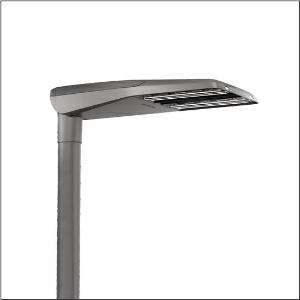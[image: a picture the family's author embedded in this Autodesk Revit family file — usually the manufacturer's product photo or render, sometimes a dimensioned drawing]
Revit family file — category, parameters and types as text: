
# Revit family: streetlight_sl_11_iq_midi___st1_2p1_0_5xc3g41e08me_f4ca
name_source: partatom
category: Lighting Fixtures
units: mm (PartAtom-declared; Revit-internal decimal feet)

## family parameters
Cut with Voids When Loaded = No
Host = Face
Light Source = No
Part Type = Normal
Room Calculation Point = No
Round Connector Dimension = Use Diameter
Shared = No

## types (1)
- --- (1 x LED, 18520 lm, 121.7 W, 4000K)
    Apparent Load = 122 VA
    CIE Flux Codes = 31 68 95 100 100
    Color Rendering = 70
    Color Temperature = 4000K
    Default Elevation = 1800 mm
    Description = Streetlight SL 11 iQ midi, mast luminaire, primary light control with 3 zone facetted reflector, of plastic, silver coated, highly specular, primary optical cover: cover, of PMMA, transparent, light distribution: ST1.2P1.0, light emission: direct distribution, primary light characteristic: asymmetric, installation type: post-top, side-entry, LED, High Power LED, rated luminous flux: 18.520lm, luminous efficacy: 152lm/W, light colour: 740, colour temperature: 4000K, control: optimised constant luminous flux control (CLO 2.0), Desk-Remote (wireless, voltage-free reading and setting of iQ features in the workshop via application-optimized NFC function/RFID function), Light-Fading, Smart-Wire, Night-Set, Lumen-Switch, Temp-Guard, Auto-Match, with cable H07RN-F 5x 1.5mm², mains connection: 230..240V, AC, 50/60Hz, connection cable pre-assembled, cable length: 12,5m, start of lifetime: 122W, end of service life: 129W, reduction: 56W, luminaire housing, of diecast aluminium, powder-coated, Siteco® metallic grey (DB 702S), please order mast flange separately, inclination adjustable without tools: 0°, 5°, 10°, 15° (post-top) | 0°, -5°, -10°, -15° (side-entry), sealing non-destructively replaceable, multi-level sealing system, length: 780mm, width: 376mm, height: 118mm, mast flange for spigot size: 42mm (side-entry): 5XC10008XM4, 60/48mm (side-entry/post-top): 5XC10108XM2, 76/60mm (side-entry/post-top): 5XC10108XM1, equipment: Power, protection rating (complete): IP66, insulation class (complete): insulation class II (safety insulation), certification: CE, ENEC, VDE, impact resistance: IK09, permissible operating ambient temperature for outdoor applications: -25..+50°C, standard-compliant lighting for roads and squares, Environmental Product Declaration (EPD) tested and certified by an independent institute, packaging unit: 1 piece

Light Distribution: ST1.2P1.0
    Height = 118 mm
    Lamp = 1 x LED
    Lamp Light Flux = 18520 lm
    Lamp Power = 121.7 W
    Lamp count = 1
    Length = 780 mm
    Luminous efficacy = 152 lm/W
    Manufacturer = Siteco
    ModVariant = No
    Model = 5XC3G41E08ME
    Number of Poles = 1
    OnlyDefault = Yes
    Power Factor = 1
    Product Name = Streetlight SL 11 iQ midi | ST1.2P1.0
    Product group = mast luminaire | pylon top
    ProductGroupID = 6100
    Protection Class = Protection class II
    Protection Degree = IP 66
    RLX_Detail_Level = 1
    RLX_Emergency_Light_Flux = 0 lm
    RLX_Emergency_Type = 0
    RLX_Emergency_Type_DB = No
    RlxData = <blob elided: 29705 chars, md5=554db31f>
    Socket = socket
    Standby Power = 0 W
    System Light Flux = 18520 lm
    System Power = 122 W
    Type Comments = factory setting: luminous flux: 100 % | dim-lin: 254 | 544 mA
    Type Image = l_1005960.jpg
    URL = http://relux.com
    VarID = @adj_005059
    Voltage = 0 V
    Weight = 0.00 kg
    Width = 376 mm

## geometry (parser evidence)
native form markers: Blend x4, Sweep x9
no freeform markers — native parametric forms only
